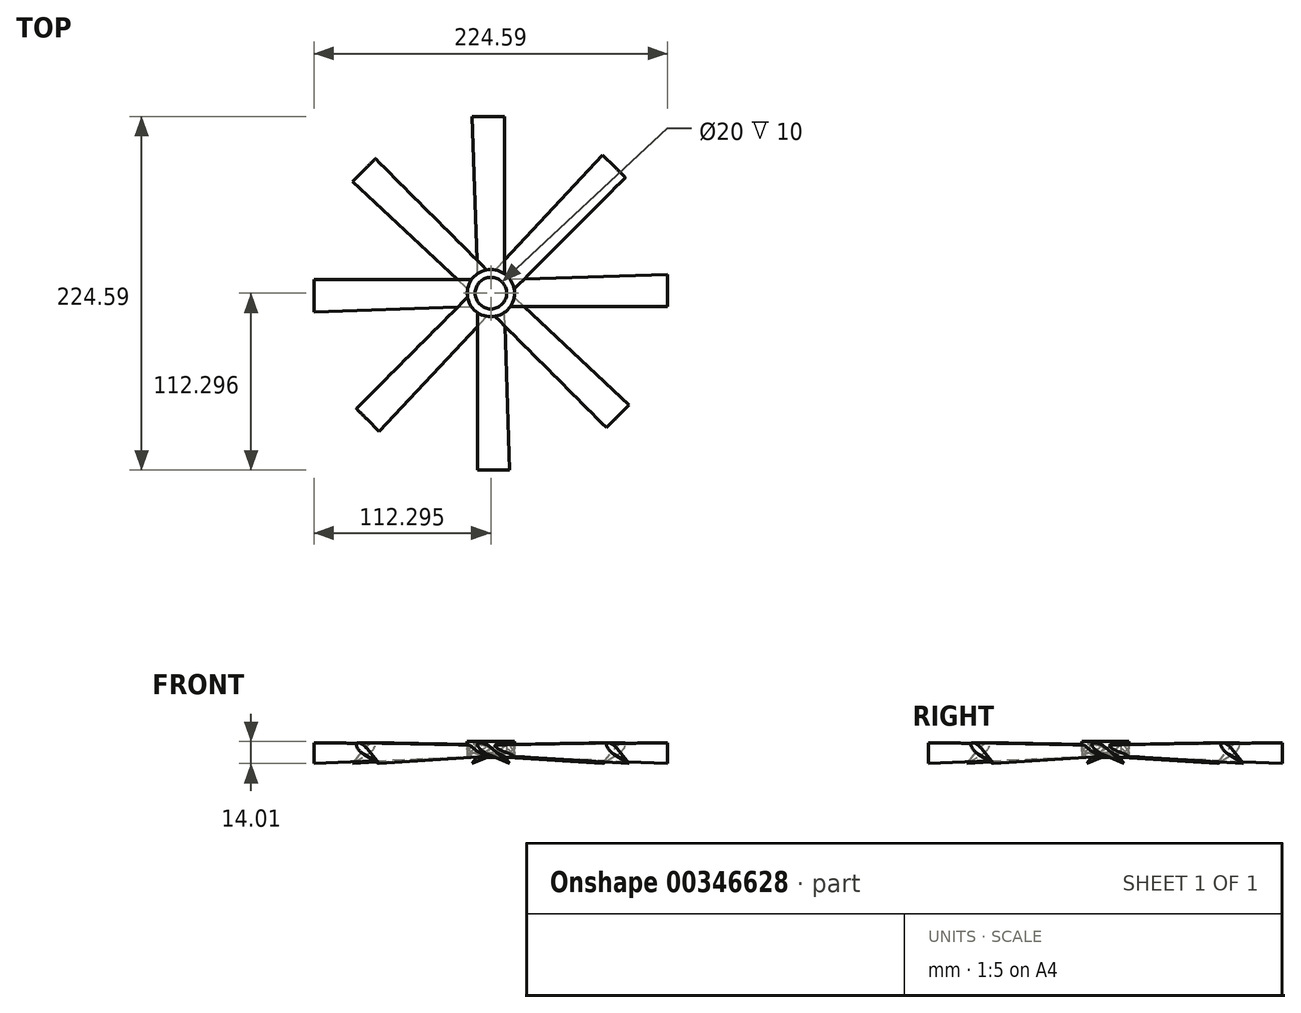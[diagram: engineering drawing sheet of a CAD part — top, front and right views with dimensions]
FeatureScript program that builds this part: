
annotation { "Feature Type Name" : "Feature", "Feature Type Description" : "" }
export const myFeature = defineFeature(function(context is Context, id is Id, definition is map)
    precondition{}
    {
        {
            var Q0;
            Q0=qCreatedBy(makeId("Right.planeOp"),FACE);
            var sketch = newSketch(context, id + "F0", { "sketchPlane" : qUnion([Q0])});
            skCircle(sketch, "E0", {"center": v(0, 0) * mm, "radius": 5 * mm});
            skPoint(sketch, "E1", {"position": v(3.38, 3.68) * mm});
            skPoint(sketch, "E2", {"position": v(-2.55, 4.3) * mm});
            skPoint(sketch, "E3", {"position": v(-4.58, 2) * mm});
            skPoint(sketch, "E4", {"position": v(-3.59, -3.48) * mm});
            skPoint(sketch, "E5", {"position": v(1.45, -4.79) * mm});
            skLineSegment(sketch, "E6", {"start": v(0, 11.08) * mm, "end": v(0, 16.41) * mm, "construction": true});
            skSolve(sketch);
        }
        {
            var Q0;
            Q0=qCreatedBy(makeId("Right.planeOp"),FACE);
            cPlane(context, id + "F1", {"entities" : qUnion([Q0]), "cplaneType" : CPlaneType.OFFSET, "offset" : 10 * mm, "width" : 150 * mm, "height" : 150 * mm});
        }
        {
            var Q0;
            Q0=qCreatedBy(id+"F1.planeOp",FACE);
            var sketch = newSketch(context, id + "F2", { "sketchPlane" : qUnion([Q0])});
            skCircle(sketch, "E7", {"center": v(0, 0) * mm, "radius": 5 * mm});
            skPoint(sketch, "E8", {"position": v(3.38, 3.68) * mm});
            skPoint(sketch, "E9", {"position": v(-2.55, 4.3) * mm});
            skPoint(sketch, "E10", {"position": v(-4.58, 2) * mm});
            skPoint(sketch, "E11", {"position": v(-3.59, -3.48) * mm});
            skPoint(sketch, "E12", {"position": v(1.45, -4.79) * mm});
            skSolve(sketch);
        }
        {
            var Q0;
            Q0=qCreatedBy(makeId("Right.planeOp"),FACE);
            cPlane(context, id + "F3", {"entities" : qUnion([Q0]), "cplaneType" : CPlaneType.OFFSET, "offset" : 20 * mm, "width" : 150 * mm, "height" : 150 * mm});
        }
        {
            var Q0;
            Q0=qCreatedBy(id+"F3.planeOp",FACE);
            var sketch = newSketch(context, id + "F4", { "sketchPlane" : qUnion([Q0])});
            skLineSegment(sketch, "E13", {"start": v(11.65, 0) * mm, "end": v(19.56, 0) * mm, "construction": true});
            skLineSegment(sketch, "E14", {"start": v(-14.42, -9) * mm, "end": v(5.84, 3.65) * mm, "construction": true});
            skPoint(sketch, "E15", {"position": v(0.08, 0.05) * mm});
            skEllipse(sketch, "E16", {"center": v(0.08, 0.05) * mm, "majorRadius": 6.78 * mm, "minorRadius": 2.5 * mm, "majorAxis": v(0.85, 0.53)});
            skLineSegment(sketch, "E17", {"start": v(0.08, 0.05) * mm, "end": v(-1.24, 2.17) * mm, "construction": true});
            skLineSegment(sketch, "E18", {"start": v(-14.42, -9) * mm, "end": v(-3.41, 0.57) * mm});
            skLineSegment(sketch, "E19", {"start": v(-14.42, -9) * mm, "end": v(-0.98, -3.32) * mm});
            skPoint(sketch, "E20", {"position": v(0, 0) * mm});
            skSolve(sketch);
        }
        {
            var Q0;
            Q0=qCreatedBy(makeId("Right.planeOp"),FACE);
            cPlane(context, id + "F5", {"entities" : qUnion([Q0]), "cplaneType" : CPlaneType.OFFSET, "offset" : 25 * mm, "width" : 150 * mm, "height" : 150 * mm});
        }
        {
            var Q0;
            Q0=qCreatedBy(id+"F5.planeOp",FACE);
            var sketch = newSketch(context, id + "F6", { "sketchPlane" : qUnion([Q0])});
            skLineSegment(sketch, "E21", {"start": v(11.65, 0) * mm, "end": v(19.56, 0) * mm, "construction": true});
            skLineSegment(sketch, "E22", {"start": v(-14.28, -8.75) * mm, "end": v(3.41, 2.09) * mm, "construction": true});
            skPoint(sketch, "E23", {"position": v(0.09, 0.05) * mm});
            skEllipse(sketch, "E24", {"center": v(0.09, 0.05) * mm, "majorRadius": 3.9 * mm, "minorRadius": 2.3 * mm, "majorAxis": v(0.85, 0.52)});
            skLineSegment(sketch, "E25", {"start": v(0.09, 0.05) * mm, "end": v(-1.12, 2.01) * mm, "construction": true});
            skLineSegment(sketch, "E26", {"start": v(-14.28, -8.75) * mm, "end": v(-1.85, 1.49) * mm});
            skLineSegment(sketch, "E27", {"start": v(-14.28, -8.75) * mm, "end": v(0.48, -2.33) * mm});
            skPoint(sketch, "E28", {"position": v(0, 0) * mm});
            skSolve(sketch);
        }
        {
            var Q0;
            Q0=qCreatedBy(makeId("Right.planeOp"),FACE);
            cPlane(context, id + "F7", {"entities" : qUnion([Q0]), "cplaneType" : CPlaneType.OFFSET, "offset" : 30 * mm, "width" : 150 * mm, "height" : 150 * mm});
        }
        {
            var Q0;
            Q0=qCreatedBy(id+"F7.planeOp",FACE);
            var sketch = newSketch(context, id + "F8", { "sketchPlane" : qUnion([Q0])});
            skLineSegment(sketch, "E29", {"start": v(11.65, 0) * mm, "end": v(19.56, 0) * mm, "construction": true});
            skLineSegment(sketch, "E30", {"start": v(-14.14, -8.5) * mm, "end": v(5.57, 3.35) * mm, "construction": true});
            skPoint(sketch, "E31", {"position": v(0.17, 0.1) * mm});
            skEllipse(sketch, "E32", {"center": v(0.17, 0.1) * mm, "majorRadius": 6.3 * mm, "minorRadius": 2.4 * mm, "majorAxis": v(0.86, 0.52)});
            skLineSegment(sketch, "E33", {"start": v(0.17, 0.1) * mm, "end": v(-1.06, 2.16) * mm, "construction": true});
            skLineSegment(sketch, "E34", {"start": v(-14.14, -8.5) * mm, "end": v(-3.01, 0.78) * mm});
            skLineSegment(sketch, "E35", {"start": v(-14.14, -8.5) * mm, "end": v(-0.72, -3.03) * mm});
            skPoint(sketch, "E36", {"position": v(0, 0) * mm});
            skSolve(sketch);
        }
        {
            var Q0;
            Q0=qCreatedBy(makeId("Right.planeOp"),FACE);
            cPlane(context, id + "F9", {"entities" : qUnion([Q0]), "cplaneType" : CPlaneType.OFFSET, "offset" : 35 * mm, "width" : 150 * mm, "height" : 150 * mm});
        }
        {
            var Q0;
            Q0=qCreatedBy(id+"F9.planeOp",FACE);
            var sketch = newSketch(context, id + "F10", { "sketchPlane" : qUnion([Q0])});
            skLineSegment(sketch, "E37", {"start": v(11.65, 0) * mm, "end": v(19.56, 0) * mm, "construction": true});
            skLineSegment(sketch, "E38", {"start": v(-14, -8.25) * mm, "end": v(3.45, 2.03) * mm, "construction": true});
            skPoint(sketch, "E39", {"position": v(0.09, 0.05) * mm});
            skEllipse(sketch, "E40", {"center": v(0.09, 0.05) * mm, "majorRadius": 3.9 * mm, "minorRadius": 2.2 * mm, "majorAxis": v(0.86, 0.5)});
            skLineSegment(sketch, "E41", {"start": v(0.09, 0.05) * mm, "end": v(-1.03, 1.95) * mm, "construction": true});
            skLineSegment(sketch, "E42", {"start": v(-14, -8.25) * mm, "end": v(-1.8, 1.42) * mm});
            skLineSegment(sketch, "E43", {"start": v(-14, -8.25) * mm, "end": v(0.37, -2.26) * mm});
            skPoint(sketch, "E44", {"position": v(0, 0) * mm});
            skSolve(sketch);
        }
        {
            var Q0;
            Q0=qCreatedBy(makeId("Right.planeOp"),FACE);
            cPlane(context, id + "F11", {"entities" : qUnion([Q0]), "cplaneType" : CPlaneType.OFFSET, "offset" : 40 * mm, "width" : 150 * mm, "height" : 150 * mm});
        }
        {
            var Q0;
            Q0=qCreatedBy(id+"F11.planeOp",FACE);
            var sketch = newSketch(context, id + "F12", { "sketchPlane" : qUnion([Q0])});
            skLineSegment(sketch, "E45", {"start": v(11.65, 0) * mm, "end": v(19.56, 0) * mm, "construction": true});
            skLineSegment(sketch, "E46", {"start": v(-13.86, -8) * mm, "end": v(5.63, 3.25) * mm, "construction": true});
            skPoint(sketch, "E47", {"position": v(0.26, 0.15) * mm});
            skEllipse(sketch, "E48", {"center": v(0.26, 0.15) * mm, "majorRadius": 6.2 * mm, "minorRadius": 2.3 * mm, "majorAxis": v(0.87, 0.5)});
            skLineSegment(sketch, "E49", {"start": v(0.26, 0.15) * mm, "end": v(-0.9, 2.14) * mm, "construction": true});
            skLineSegment(sketch, "E50", {"start": v(-13.86, -8) * mm, "end": v(-2.85, 0.81) * mm});
            skLineSegment(sketch, "E51", {"start": v(-13.86, -8) * mm, "end": v(-0.72, -2.87) * mm});
            skPoint(sketch, "E52", {"position": v(0, 0) * mm});
            skSolve(sketch);
        }
        {
            var Q0;
            Q0=qCreatedBy(makeId("Right.planeOp"),FACE);
            cPlane(context, id + "F13", {"entities" : qUnion([Q0]), "cplaneType" : CPlaneType.OFFSET, "offset" : 45 * mm, "width" : 150 * mm, "height" : 150 * mm});
        }
        {
            var Q0;
            Q0=qCreatedBy(id+"F13.planeOp",FACE);
            var sketch = newSketch(context, id + "F14", { "sketchPlane" : qUnion([Q0])});
            skLineSegment(sketch, "E53", {"start": v(11.65, 0) * mm, "end": v(19.56, 0) * mm, "construction": true});
            skLineSegment(sketch, "E54", {"start": v(-13.7, -7.76) * mm, "end": v(3.48, 1.97) * mm, "construction": true});
            skPoint(sketch, "E55", {"position": v(0.09, 0.05) * mm});
            skEllipse(sketch, "E56", {"center": v(0.09, 0.05) * mm, "majorRadius": 3.9 * mm, "minorRadius": 2.1 * mm, "majorAxis": v(0.87, 0.5)});
            skLineSegment(sketch, "E57", {"start": v(0.09, 0.05) * mm, "end": v(-0.95, 1.88) * mm, "construction": true});
            skLineSegment(sketch, "E58", {"start": v(-13.7, -7.76) * mm, "end": v(-1.75, 1.35) * mm});
            skLineSegment(sketch, "E59", {"start": v(-13.7, -7.76) * mm, "end": v(0.25, -2.2) * mm});
            skPoint(sketch, "E60", {"position": v(0, 0) * mm});
            skSolve(sketch);
        }
        {
            var Q0;
            Q0=qCreatedBy(makeId("Right.planeOp"),FACE);
            cPlane(context, id + "F15", {"entities" : qUnion([Q0]), "cplaneType" : CPlaneType.OFFSET, "offset" : 50 * mm, "width" : 150 * mm, "height" : 150 * mm});
        }
        {
            var Q0;
            Q0=qCreatedBy(id+"F15.planeOp",FACE);
            var sketch = newSketch(context, id + "F16", { "sketchPlane" : qUnion([Q0])});
            skLineSegment(sketch, "E61", {"start": v(11.65, 0) * mm, "end": v(19.56, 0) * mm, "construction": true});
            skLineSegment(sketch, "E62", {"start": v(-13.56, -7.51) * mm, "end": v(5.69, 3.15) * mm, "construction": true});
            skPoint(sketch, "E63", {"position": v(0.35, 0.2) * mm});
            skEllipse(sketch, "E64", {"center": v(0.35, 0.2) * mm, "majorRadius": 6.1 * mm, "minorRadius": 2.2 * mm, "majorAxis": v(0.87, 0.48)});
            skLineSegment(sketch, "E65", {"start": v(0.35, 0.2) * mm, "end": v(-0.72, 2.12) * mm, "construction": true});
            skLineSegment(sketch, "E66", {"start": v(-13.56, -7.51) * mm, "end": v(-2.68, 0.84) * mm});
            skLineSegment(sketch, "E67", {"start": v(-13.56, -7.51) * mm, "end": v(-0.71, -2.72) * mm});
            skPoint(sketch, "E68", {"position": v(0, 0) * mm});
            skSolve(sketch);
        }
        {
            var Q0;
            Q0=qCreatedBy(makeId("Right.planeOp"),FACE);
            cPlane(context, id + "F17", {"entities" : qUnion([Q0]), "cplaneType" : CPlaneType.OFFSET, "offset" : 55 * mm, "width" : 150 * mm, "height" : 150 * mm});
        }
        {
            var Q0;
            Q0=qCreatedBy(id+"F17.planeOp",FACE);
            var sketch = newSketch(context, id + "F18", { "sketchPlane" : qUnion([Q0])});
            skLineSegment(sketch, "E69", {"start": v(11.65, 0) * mm, "end": v(19.56, 0) * mm, "construction": true});
            skLineSegment(sketch, "E70", {"start": v(-13.4, -7.28) * mm, "end": v(3.52, 1.9) * mm, "construction": true});
            skPoint(sketch, "E71", {"position": v(0.09, 0.05) * mm});
            skEllipse(sketch, "E72", {"center": v(0.09, 0.05) * mm, "majorRadius": 3.9 * mm, "minorRadius": 2 * mm, "majorAxis": v(0.88, 0.48)});
            skLineSegment(sketch, "E73", {"start": v(0.09, 0.05) * mm, "end": v(-0.87, 1.8) * mm, "construction": true});
            skLineSegment(sketch, "E74", {"start": v(-13.4, -7.28) * mm, "end": v(-1.7, 1.27) * mm});
            skLineSegment(sketch, "E75", {"start": v(-13.4, -7.28) * mm, "end": v(0.14, -2.13) * mm});
            skPoint(sketch, "E76", {"position": v(0, 0) * mm});
            skSolve(sketch);
        }
        {
            var Q0;
            Q0=qCreatedBy(makeId("Right.planeOp"),FACE);
            cPlane(context, id + "F19", {"entities" : qUnion([Q0]), "cplaneType" : CPlaneType.OFFSET, "offset" : 60 * mm, "width" : 150 * mm, "height" : 150 * mm});
        }
        {
            var Q0;
            Q0=qCreatedBy(id+"F19.planeOp",FACE);
            var sketch = newSketch(context, id + "F20", { "sketchPlane" : qUnion([Q0])});
            skLineSegment(sketch, "E77", {"start": v(11.65, 0) * mm, "end": v(19.56, 0) * mm, "construction": true});
            skLineSegment(sketch, "E78", {"start": v(-13.24, -7.04) * mm, "end": v(5.74, 3.05) * mm, "construction": true});
            skPoint(sketch, "E79", {"position": v(0.44, 0.23) * mm});
            skEllipse(sketch, "E80", {"center": v(0.44, 0.23) * mm, "majorRadius": 6 * mm, "minorRadius": 2.1 * mm, "majorAxis": v(0.88, 0.47)});
            skLineSegment(sketch, "E81", {"start": v(0.44, 0.23) * mm, "end": v(-0.54, 2.09) * mm, "construction": true});
            skLineSegment(sketch, "E82", {"start": v(-13.24, -7.04) * mm, "end": v(-2.52, 0.85) * mm});
            skLineSegment(sketch, "E83", {"start": v(-13.24, -7.04) * mm, "end": v(-0.7, -2.57) * mm});
            skPoint(sketch, "E84", {"position": v(0, 0) * mm});
            skSolve(sketch);
        }
        {
            var Q0;
            Q0=qCreatedBy(makeId("Right.planeOp"),FACE);
            cPlane(context, id + "F21", {"entities" : qUnion([Q0]), "cplaneType" : CPlaneType.OFFSET, "offset" : 65 * mm, "width" : 150 * mm, "height" : 150 * mm});
        }
        {
            var Q0;
            Q0=qCreatedBy(id+"F21.planeOp",FACE);
            var sketch = newSketch(context, id + "F22", { "sketchPlane" : qUnion([Q0])});
            skLineSegment(sketch, "E85", {"start": v(11.65, 0) * mm, "end": v(19.56, 0) * mm, "construction": true});
            skLineSegment(sketch, "E86", {"start": v(-13.08, -6.81) * mm, "end": v(3.55, 1.85) * mm, "construction": true});
            skPoint(sketch, "E87", {"position": v(0.09, 0.05) * mm});
            skEllipse(sketch, "E88", {"center": v(0.09, 0.05) * mm, "majorRadius": 3.9 * mm, "minorRadius": 1.9 * mm, "majorAxis": v(0.89, 0.46)});
            skLineSegment(sketch, "E89", {"start": v(0.09, 0.05) * mm, "end": v(-0.79, 1.73) * mm, "construction": true});
            skLineSegment(sketch, "E90", {"start": v(-13.08, -6.81) * mm, "end": v(-1.67, 1.2) * mm});
            skLineSegment(sketch, "E91", {"start": v(-13.08, -6.81) * mm, "end": v(0.03, -2.05) * mm});
            skPoint(sketch, "E92", {"position": v(0, 0) * mm});
            skSolve(sketch);
        }
        {
            var Q0;
            Q0=qCreatedBy(makeId("Right.planeOp"),FACE);
            cPlane(context, id + "F23", {"entities" : qUnion([Q0]), "cplaneType" : CPlaneType.OFFSET, "offset" : 70 * mm, "width" : 150 * mm, "height" : 150 * mm});
        }
        {
            var Q0;
            Q0=qCreatedBy(id+"F23.planeOp",FACE);
            var sketch = newSketch(context, id + "F24", { "sketchPlane" : qUnion([Q0])});
            skLineSegment(sketch, "E93", {"start": v(11.65, 0) * mm, "end": v(19.56, 0) * mm, "construction": true});
            skLineSegment(sketch, "E94", {"start": v(-12.92, -6.58) * mm, "end": v(5.8, 2.95) * mm, "construction": true});
            skPoint(sketch, "E95", {"position": v(0.53, 0.27) * mm});
            skEllipse(sketch, "E96", {"center": v(0.53, 0.27) * mm, "majorRadius": 5.9 * mm, "minorRadius": 2 * mm, "majorAxis": v(0.9, 0.45)});
            skLineSegment(sketch, "E97", {"start": v(0.53, 0.27) * mm, "end": v(-0.37, 2.05) * mm, "construction": true});
            skLineSegment(sketch, "E98", {"start": v(-12.92, -6.58) * mm, "end": v(-2.36, 0.87) * mm});
            skLineSegment(sketch, "E99", {"start": v(-12.92, -6.58) * mm, "end": v(-0.68, -2.41) * mm});
            skPoint(sketch, "E100", {"position": v(0, 0) * mm});
            skSolve(sketch);
        }
        {
            var Q0;
            Q0=qCreatedBy(makeId("Right.planeOp"),FACE);
            cPlane(context, id + "F25", {"entities" : qUnion([Q0]), "cplaneType" : CPlaneType.OFFSET, "offset" : 75 * mm, "width" : 150 * mm, "height" : 150 * mm});
        }
        {
            var Q0;
            Q0=qCreatedBy(id+"F25.planeOp",FACE);
            var sketch = newSketch(context, id + "F26", { "sketchPlane" : qUnion([Q0])});
            skLineSegment(sketch, "E101", {"start": v(11.65, 0) * mm, "end": v(19.56, 0) * mm, "construction": true});
            skLineSegment(sketch, "E102", {"start": v(-12.75, -6.36) * mm, "end": v(3.58, 1.78) * mm, "construction": true});
            skPoint(sketch, "E103", {"position": v(0.09, 0.04) * mm});
            skEllipse(sketch, "E104", {"center": v(0.09, 0.04) * mm, "majorRadius": 3.9 * mm, "minorRadius": 1.8 * mm, "majorAxis": v(0.9, 0.45)});
            skLineSegment(sketch, "E105", {"start": v(0.09, 0.04) * mm, "end": v(-0.71, 1.66) * mm, "construction": true});
            skLineSegment(sketch, "E106", {"start": v(-12.75, -6.36) * mm, "end": v(-1.63, 1.12) * mm});
            skLineSegment(sketch, "E107", {"start": v(-12.75, -6.36) * mm, "end": v(-0.09, -1.98) * mm});
            skPoint(sketch, "E108", {"position": v(0, 0) * mm});
            skSolve(sketch);
        }
        {
            var Q0;
            Q0=qCreatedBy(makeId("Right.planeOp"),FACE);
            cPlane(context, id + "F27", {"entities" : qUnion([Q0]), "cplaneType" : CPlaneType.OFFSET, "offset" : 80 * mm, "width" : 150 * mm, "height" : 150 * mm});
        }
        {
            var Q0;
            Q0=qCreatedBy(id+"F27.planeOp",FACE);
            var sketch = newSketch(context, id + "F28", { "sketchPlane" : qUnion([Q0])});
            skLineSegment(sketch, "E109", {"start": v(11.65, 0) * mm, "end": v(19.56, 0) * mm, "construction": true});
            skLineSegment(sketch, "E110", {"start": v(-12.58, -6.14) * mm, "end": v(5.84, 2.85) * mm, "construction": true});
            skPoint(sketch, "E111", {"position": v(0.63, 0.3) * mm});
            skEllipse(sketch, "E112", {"center": v(0.63, 0.3) * mm, "majorRadius": 5.8 * mm, "minorRadius": 1.9 * mm, "majorAxis": v(0.9, 0.44)});
            skLineSegment(sketch, "E113", {"start": v(0.63, 0.3) * mm, "end": v(-0.2, 2.01) * mm, "construction": true});
            skLineSegment(sketch, "E114", {"start": v(-12.58, -6.14) * mm, "end": v(-2.2, 0.87) * mm});
            skLineSegment(sketch, "E115", {"start": v(-12.58, -6.14) * mm, "end": v(-0.66, -2.27) * mm});
            skPoint(sketch, "E116", {"position": v(0, 0) * mm});
            skSolve(sketch);
        }
        {
            var Q0;
            Q0=qCreatedBy(makeId("Right.planeOp"),FACE);
            cPlane(context, id + "F29", {"entities" : qUnion([Q0]), "cplaneType" : CPlaneType.OFFSET, "offset" : 85 * mm, "width" : 150 * mm, "height" : 150 * mm});
        }
        {
            var Q0;
            Q0=qCreatedBy(id+"F29.planeOp",FACE);
            var sketch = newSketch(context, id + "F30", { "sketchPlane" : qUnion([Q0])});
            skLineSegment(sketch, "E117", {"start": v(11.65, 0) * mm, "end": v(19.56, 0) * mm, "construction": true});
            skLineSegment(sketch, "E118", {"start": v(-12.41, -5.92) * mm, "end": v(3.61, 1.72) * mm, "construction": true});
            skPoint(sketch, "E119", {"position": v(0.1, 0.04) * mm});
            skEllipse(sketch, "E120", {"center": v(0.1, 0.04) * mm, "majorRadius": 3.9 * mm, "minorRadius": 1.7 * mm, "majorAxis": v(0.9, 0.43)});
            skLineSegment(sketch, "E121", {"start": v(0.1, 0.04) * mm, "end": v(-0.64, 1.58) * mm, "construction": true});
            skLineSegment(sketch, "E122", {"start": v(-12.41, -5.92) * mm, "end": v(-1.6, 1.04) * mm});
            skLineSegment(sketch, "E123", {"start": v(-12.41, -5.92) * mm, "end": v(-0.2, -1.9) * mm});
            skPoint(sketch, "E124", {"position": v(0, 0) * mm});
            skSolve(sketch);
        }
        {
            var Q0;
            Q0=qCreatedBy(makeId("Right.planeOp"),FACE);
            cPlane(context, id + "F31", {"entities" : qUnion([Q0]), "cplaneType" : CPlaneType.OFFSET, "offset" : 90 * mm, "width" : 150 * mm, "height" : 150 * mm});
        }
        {
            var Q0;
            Q0=qCreatedBy(id+"F31.planeOp",FACE);
            var sketch = newSketch(context, id + "F32", { "sketchPlane" : qUnion([Q0])});
            skLineSegment(sketch, "E125", {"start": v(11.65, 0) * mm, "end": v(19.56, 0) * mm, "construction": true});
            skLineSegment(sketch, "E126", {"start": v(-12.24, -5.7) * mm, "end": v(5.9, 2.75) * mm, "construction": true});
            skPoint(sketch, "E127", {"position": v(0.73, 0.34) * mm});
            skEllipse(sketch, "E128", {"center": v(0.73, 0.34) * mm, "majorRadius": 5.7 * mm, "minorRadius": 1.8 * mm, "majorAxis": v(0.9, 0.42)});
            skLineSegment(sketch, "E129", {"start": v(0.73, 0.34) * mm, "end": v(-0.04, 1.97) * mm, "construction": true});
            skLineSegment(sketch, "E130", {"start": v(-12.24, -5.7) * mm, "end": v(-2.03, 0.87) * mm});
            skLineSegment(sketch, "E131", {"start": v(-12.24, -5.7) * mm, "end": v(-0.64, -2.12) * mm});
            skPoint(sketch, "E132", {"position": v(0, 0) * mm});
            skSolve(sketch);
        }
        {
            var Q0;
            Q0=qCreatedBy(makeId("Right.planeOp"),FACE);
            cPlane(context, id + "F33", {"entities" : qUnion([Q0]), "cplaneType" : CPlaneType.OFFSET, "offset" : 95 * mm, "width" : 150 * mm, "height" : 150 * mm});
        }
        {
            var Q0;
            Q0=qCreatedBy(id+"F33.planeOp",FACE);
            var sketch = newSketch(context, id + "F34", { "sketchPlane" : qUnion([Q0])});
            skLineSegment(sketch, "E133", {"start": v(11.65, 0) * mm, "end": v(19.56, 0) * mm, "construction": true});
            skLineSegment(sketch, "E134", {"start": v(-12.06, -5.5) * mm, "end": v(3.64, 1.66) * mm, "construction": true});
            skPoint(sketch, "E135", {"position": v(0.1, 0.04) * mm});
            skEllipse(sketch, "E136", {"center": v(0.1, 0.04) * mm, "majorRadius": 3.9 * mm, "minorRadius": 1.6 * mm, "majorAxis": v(0.9, 0.41)});
            skLineSegment(sketch, "E137", {"start": v(0.1, 0.04) * mm, "end": v(-0.57, 1.5) * mm, "construction": true});
            skLineSegment(sketch, "E138", {"start": v(-12.06, -5.5) * mm, "end": v(-1.58, 0.96) * mm});
            skLineSegment(sketch, "E139", {"start": v(-12.06, -5.5) * mm, "end": v(-0.31, -1.82) * mm});
            skPoint(sketch, "E140", {"position": v(0, 0) * mm});
            skSolve(sketch);
        }
        {
            var Q0;
            Q0=qCreatedBy(makeId("Right.planeOp"),FACE);
            cPlane(context, id + "F35", {"entities" : qUnion([Q0]), "cplaneType" : CPlaneType.OFFSET, "offset" : 100 * mm, "width" : 150 * mm, "height" : 150 * mm});
        }
        {
            var Q0;
            Q0=qCreatedBy(id+"F35.planeOp",FACE);
            var sketch = newSketch(context, id + "F36", { "sketchPlane" : qUnion([Q0])});
            skLineSegment(sketch, "E141", {"start": v(11.65, 0) * mm, "end": v(19.56, 0) * mm, "construction": true});
            skLineSegment(sketch, "E142", {"start": v(-11.88, -5.29) * mm, "end": v(5.94, 2.64) * mm, "construction": true});
            skPoint(sketch, "E143", {"position": v(0.82, 0.37) * mm});
            skEllipse(sketch, "E144", {"center": v(0.82, 0.37) * mm, "majorRadius": 5.6 * mm, "minorRadius": 1.7 * mm, "majorAxis": v(0.91, 0.4)});
            skLineSegment(sketch, "E145", {"start": v(0.82, 0.37) * mm, "end": v(0.13, 1.92) * mm, "construction": true});
            skLineSegment(sketch, "E146", {"start": v(-11.88, -5.29) * mm, "end": v(-1.87, 0.87) * mm});
            skLineSegment(sketch, "E147", {"start": v(-11.88, -5.29) * mm, "end": v(-0.6, -1.97) * mm});
            skPoint(sketch, "E148", {"position": v(0, 0) * mm});
            skSolve(sketch);
        }
        {
            var Q0;
            Q0=qCreatedBy(makeId("Right.planeOp"),FACE);
            cPlane(context, id + "F37", {"entities" : qUnion([Q0]), "cplaneType" : CPlaneType.OFFSET, "offset" : 105 * mm, "width" : 150 * mm, "height" : 150 * mm});
        }
        {
            var Q0;
            Q0=qCreatedBy(id+"F37.planeOp",FACE);
            var sketch = newSketch(context, id + "F38", { "sketchPlane" : qUnion([Q0])});
            skLineSegment(sketch, "E149", {"start": v(11.65, 0) * mm, "end": v(19.56, 0) * mm, "construction": true});
            skLineSegment(sketch, "E150", {"start": v(-11.7, -5.08) * mm, "end": v(3.67, 1.6) * mm, "construction": true});
            skPoint(sketch, "E151", {"position": v(0.1, 0.04) * mm});
            skEllipse(sketch, "E152", {"center": v(0.1, 0.04) * mm, "majorRadius": 3.9 * mm, "minorRadius": 1.5 * mm, "majorAxis": v(0.92, 0.4)});
            skLineSegment(sketch, "E153", {"start": v(0.1, 0.04) * mm, "end": v(-0.5, 1.42) * mm, "construction": true});
            skLineSegment(sketch, "E154", {"start": v(-11.7, -5.08) * mm, "end": v(-1.56, 0.88) * mm});
            skLineSegment(sketch, "E155", {"start": v(-11.7, -5.08) * mm, "end": v(-0.42, -1.74) * mm});
            skPoint(sketch, "E156", {"position": v(0, 0) * mm});
            skSolve(sketch);
        }
        {
            var Q0;
            Q0=qCreatedBy(makeId("Right.planeOp"),FACE);
            cPlane(context, id + "F39", {"entities" : qUnion([Q0]), "cplaneType" : CPlaneType.OFFSET, "offset" : 110 * mm, "width" : 150 * mm, "height" : 150 * mm});
        }
        {
            var Q0;
            Q0=qCreatedBy(id+"F39.planeOp",FACE);
            var sketch = newSketch(context, id + "F40", { "sketchPlane" : qUnion([Q0])});
            skLineSegment(sketch, "E157", {"start": v(11.65, 0) * mm, "end": v(19.56, 0) * mm, "construction": true});
            skLineSegment(sketch, "E158", {"start": v(-11.5, -4.88) * mm, "end": v(5.98, 2.54) * mm, "construction": true});
            skPoint(sketch, "E159", {"position": v(0.92, 0.4) * mm});
            skEllipse(sketch, "E160", {"center": v(0.92, 0.4) * mm, "majorRadius": 5.5 * mm, "minorRadius": 1.6 * mm, "majorAxis": v(0.92, 0.4)});
            skLineSegment(sketch, "E161", {"start": v(0.92, 0.4) * mm, "end": v(0.3, 1.86) * mm, "construction": true});
            skLineSegment(sketch, "E162", {"start": v(-11.5, -4.88) * mm, "end": v(-1.71, 0.86) * mm});
            skLineSegment(sketch, "E163", {"start": v(-11.5, -4.88) * mm, "end": v(-0.57, -1.83) * mm});
            skPoint(sketch, "E164", {"position": v(0, 0) * mm});
            skSolve(sketch);
        }
        {
            var Q0;
            Q0=qCreatedBy(makeId("Right.planeOp"),FACE);
            cPlane(context, id + "F41", {"entities" : qUnion([Q0]), "cplaneType" : CPlaneType.OFFSET, "offset" : 115 * mm, "width" : 150 * mm, "height" : 150 * mm});
        }
        {
            var Q0;
            Q0=qCreatedBy(id+"F41.planeOp",FACE);
            var sketch = newSketch(context, id + "F42", { "sketchPlane" : qUnion([Q0])});
            skLineSegment(sketch, "E165", {"start": v(11.65, 0) * mm, "end": v(19.56, 0) * mm, "construction": true});
            skLineSegment(sketch, "E166", {"start": v(-11.32, -4.69) * mm, "end": v(3.7, 1.53) * mm, "construction": true});
            skPoint(sketch, "E167", {"position": v(0.1, 0.04) * mm});
            skEllipse(sketch, "E168", {"center": v(0.1, 0.04) * mm, "majorRadius": 3.9 * mm, "minorRadius": 1.4 * mm, "majorAxis": v(0.92, 0.38)});
            skLineSegment(sketch, "E169", {"start": v(0.1, 0.04) * mm, "end": v(-0.44, 1.33) * mm, "construction": true});
            skLineSegment(sketch, "E170", {"start": v(-11.32, -4.69) * mm, "end": v(-1.55, 0.8) * mm});
            skLineSegment(sketch, "E171", {"start": v(-11.32, -4.69) * mm, "end": v(-0.54, -1.66) * mm});
            skPoint(sketch, "E172", {"position": v(0, 0) * mm});
            skSolve(sketch);
        }
        {
            var Q0;
            Q0=qCreatedBy(makeId("Right.planeOp"),FACE);
            cPlane(context, id + "F43", {"entities" : qUnion([Q0]), "cplaneType" : CPlaneType.OFFSET, "offset" : 120 * mm, "width" : 150 * mm, "height" : 150 * mm});
        }
        {
            var Q0;
            Q0=qCreatedBy(id+"F43.planeOp",FACE);
            var sketch = newSketch(context, id + "F44", { "sketchPlane" : qUnion([Q0])});
            skLineSegment(sketch, "E173", {"start": v(11.65, 0) * mm, "end": v(19.56, 0) * mm, "construction": true});
            skLineSegment(sketch, "E174", {"start": v(-11.13, -4.5) * mm, "end": v(6.03, 2.43) * mm, "construction": true});
            skPoint(sketch, "E175", {"position": v(1.02, 0.41) * mm});
            skEllipse(sketch, "E176", {"center": v(1.02, 0.41) * mm, "majorRadius": 5.4 * mm, "minorRadius": 1.5 * mm, "majorAxis": v(0.93, 0.37)});
            skLineSegment(sketch, "E177", {"start": v(1.02, 0.41) * mm, "end": v(0.46, 1.8) * mm, "construction": true});
            skLineSegment(sketch, "E178", {"start": v(-11.13, -4.5) * mm, "end": v(-1.56, 0.85) * mm});
            skLineSegment(sketch, "E179", {"start": v(-11.13, -4.5) * mm, "end": v(-0.53, -1.69) * mm});
            skPoint(sketch, "E180", {"position": v(0, 0) * mm});
            skLineSegment(sketch, "E181", {"start": v(0, 10.3) * mm, "end": v(0, 18.2) * mm, "construction": true});
            skSolve(sketch);
        }
        {
            var Q0;
            Q0 = qSketchRegion(id + "F4", true);
            var Q1;
            Q1 = qSketchRegion(id + "F44", true);
            loft(context, id + "F45", {"sheetProfilesArray" : [{ "sheetProfileEntities" : qUnion([Q0]) }, { "sheetProfileEntities" : qUnion([Q1]) }]});
        }
        {
            var Q0;
            Q0=qCreatedBy(makeId("Top.planeOp"),FACE);
            var sketch = newSketch(context, id + "F46", { "sketchPlane" : qUnion([Q0])});
            skCircle(sketch, "E182", {"center": v(0, 0) * mm, "radius": 7.5 * mm});
            skCircle(sketch, "E183", {"center": v(0, 0) * mm, "radius": 15 * mm});
            skPoint(sketch, "E184", {"position": v(120, 6.06) * mm});
            skPoint(sketch, "E185", {"position": v(120, -11.13) * mm});
            skLineSegment(sketch, "E186", {"start": v(120, 6.06) * mm, "end": v(120, -11.13) * mm, "construction": true});
            skPoint(sketch, "E187", {"position": v(120, -2.53) * mm});
            skCircle(sketch, "E188", {"center": v(132.3, -2.53) * mm, "radius": 15 * mm});
            skCircle(sketch, "E189", {"center": v(132.3, -2.53) * mm, "radius": 10 * mm});
            skSolve(sketch);
        }
        {
            var Q0;
            Q0=makeQuery(id+"F46.imprint","IMPRINT",FACE,{"disambiguationData":[TD([[makeQuery(id+"F46.imprint","IMPRINT",EDGE,{"derivedFrom":sQuery(id+"F46.wireOp",EDGE,"E188")}),1.0]])]});
            extrude(context, id + "F47", {"entities" : qUnion([Q0]), "operationType" : NewBodyOperationType.ADD, "depth" : 5 * mm, "offsetDistance" : 25 * mm, "hasSecondDirection" : true, "secondDirectionOppositeDirection" : true, "secondDirectionDepth" : 5 * mm});
        }
        {
            var Q0;
            {var subQ0=sQuery(id+"F44.wireOp",EDGE,"E176");var subQ1=makeQuery(id+"F44.imprint","INTERSECT",VERTEX,{"derivedFrom":[subQ0,sQuery(id+"F44.wireOp",EDGE,"E178")]});var subQ3=sQuery(id+"F4.wireOp",EDGE,"E16");var subQ4=makeQuery(id+"F4.imprint","INTERSECT",VERTEX,{"derivedFrom":[subQ3,sQuery(id+"F4.wireOp",EDGE,"E18")]});Q0=makeQuery(id+"F45.opLoft","SWEPT_BODY",BODY,{"disambiguationData":[OSD([makeQuery(id+"F4.imprint","IMPRINT",FACE,{"disambiguationData":[TD([[makeQuery(id+"F4.imprint","IMPRINT",EDGE,{"disambiguationData":[TD([[subQ4,-1.0]])],"derivedFrom":subQ3}),1.0]])]}),makeQuery(id+"F44.imprint","IMPRINT",FACE,{"disambiguationData":[TD([[makeQuery(id+"F44.imprint","IMPRINT",EDGE,{"disambiguationData":[TD([[subQ1,-1.0]])],"derivedFrom":subQ0}),1.0]])]})])]});}
            var Q1;
            Q1=sQuery(id+"F46.wireOp",EDGE,"E189");
            circularPattern(context, id + "F48", {"operationType" : NewBodyOperationType.ADD, "entities" : qUnion([Q0]), "axis" : qUnion([Q1]), "angle" : 360 * degree, "instanceCount" : 8, "equalSpace" : true});
        }
    });
